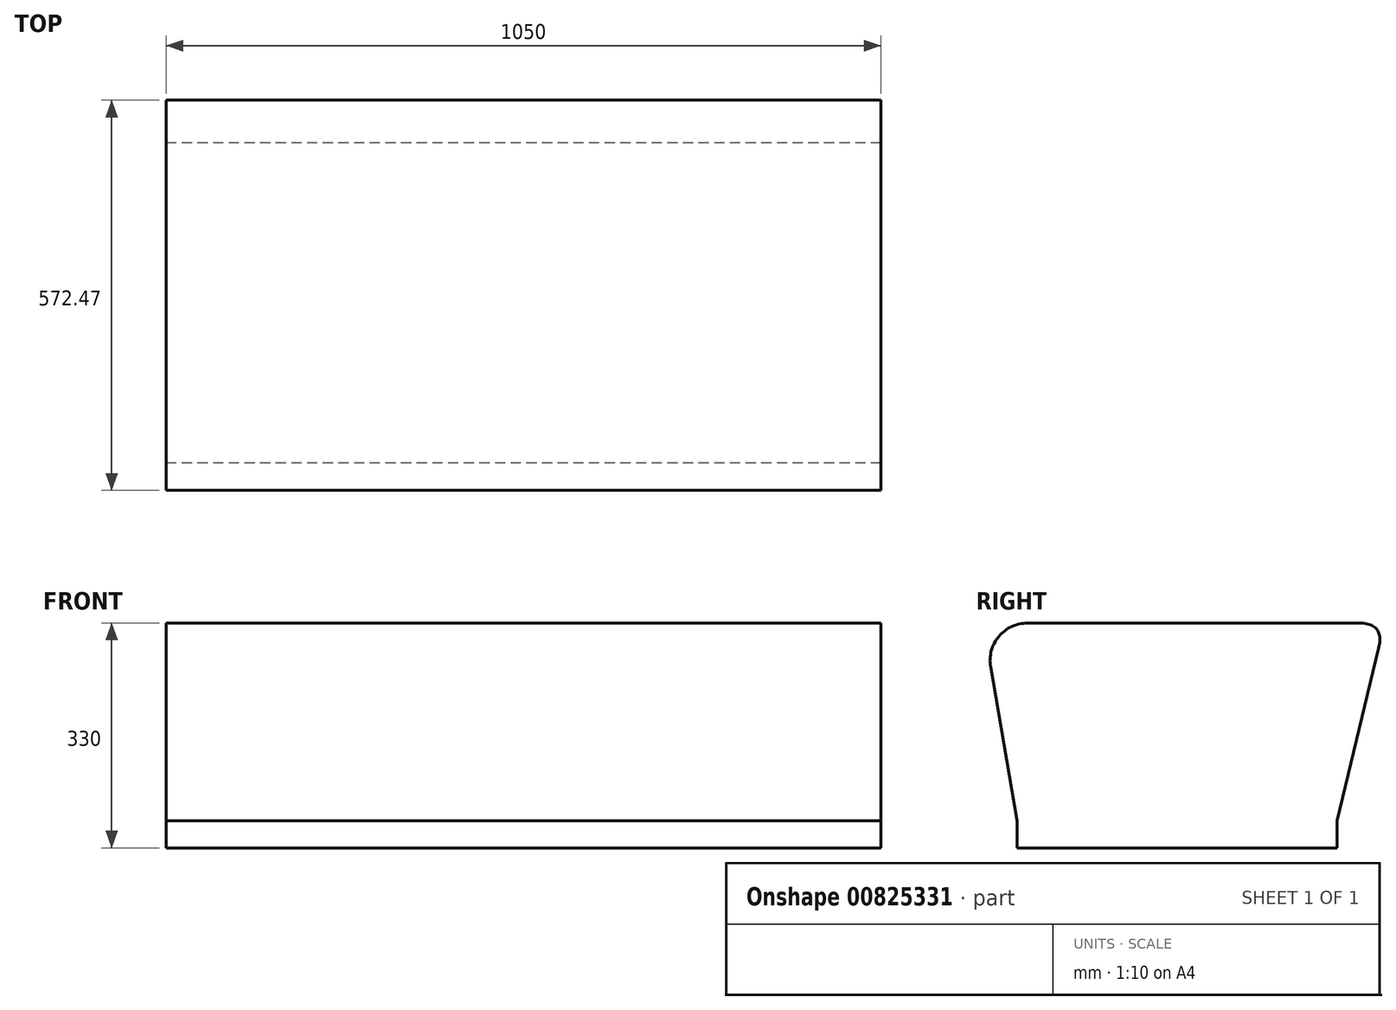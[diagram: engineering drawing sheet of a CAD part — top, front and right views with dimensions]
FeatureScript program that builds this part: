
annotation { "Feature Type Name" : "Feature", "Feature Type Description" : "" }
export const myFeature = defineFeature(function(context is Context, id is Id, definition is map)
    precondition{}
    {
        {
            var Q0;
            Q0=qCreatedBy(makeId("Right.planeOp"),FACE);
            var sketch = newSketch(context, id + "F0", { "sketchPlane" : qUnion([Q0])});
            skLineSegment(sketch, "E0", {"start": v(0, 0) * mm, "end": v(470, 0) * mm});
            skLineSegment(sketch, "E1", {"start": v(470, 0) * mm, "end": v(470, 290) * mm, "construction": true});
            skLineSegment(sketch, "E2", {"start": v(470, 290) * mm, "end": v(540, 290) * mm});
            skLineSegment(sketch, "E3", {"start": v(540, 290) * mm, "end": v(470, 290) * mm});
            skLineSegment(sketch, "E4", {"start": v(470, 290) * mm, "end": v(-50, 290) * mm});
            skLineSegment(sketch, "E5", {"start": v(-50, 290) * mm, "end": v(0, 0) * mm});
            skLineSegment(sketch, "E6", {"start": v(540, 290) * mm, "end": v(470, 0) * mm});
            skLineSegment(sketch, "E7", {"start": v(470, 0) * mm, "end": v(470, -40) * mm});
            skLineSegment(sketch, "E8", {"start": v(470, -40) * mm, "end": v(0, -40) * mm});
            skLineSegment(sketch, "E9", {"start": v(0, -40) * mm, "end": v(0, 0) * mm});
            skSolve(sketch);
        }
        {
            var Q0;
            Q0=makeQuery(id+"F0.imprint","IMPRINT",FACE,{"disambiguationData":[TD([[makeQuery(id+"F0.imprint","IMPRINT",EDGE,{"derivedFrom":sQuery(id+"F0.wireOp",EDGE,"E0")}),1.0]])]});
            var Q1;
            Q1=makeQuery(id+"F0.imprint","IMPRINT",FACE,{"disambiguationData":[TD([[makeQuery(id+"F0.imprint","IMPRINT",EDGE,{"derivedFrom":sQuery(id+"F0.wireOp",EDGE,"E0")}),-1.0]])]});
            extrude(context, id + "F1", {"entities" : qUnion([Q0, Q1]), "depth" : 1050 * mm, "offsetDistance" : 25 * mm});
        }
        {
            var Q0;
            Q0=makeQuery(id+"F1.opExtrude","SWEPT_EDGE",EDGE,{"disambiguationData":[OSD([sQuery(id+"F0.wireOp",EDGE,"E4"),sQuery(id+"F0.wireOp",EDGE,"E5")])]});
            fillet(context, id + "F2", {"entities" : qUnion([Q0]), "radius" : 55 * mm, "tangentPropagation" : true, "allowEdgeOverflow" : false});
        }
        {
            var Q0;
            Q0=makeQuery(id+"F1.opExtrude","SWEPT_EDGE",EDGE,{"disambiguationData":[OSD([sQuery(id+"F0.wireOp",EDGE,"E3"),sQuery(id+"F0.wireOp",EDGE,"E6")])]});
            fillet(context, id + "F3", {"entities" : qUnion([Q0]), "radius" : 30 * mm, "tangentPropagation" : true, "rho" : 0.5, "crossSection" : FilletCrossSection.CONIC, "allowEdgeOverflow" : false});
        }
        {
            var Q0;
            Q0=makeQuery(id+"F1.opExtrude","SWEPT_FACE",FACE,{"disambiguationData":[OSD([sQuery(id+"F0.wireOp",EDGE,"E8")])]});
            var sketch = newSketch(context, id + "F4", { "sketchPlane" : qUnion([Q0])});
            skLineSegment(sketch, "E10", {"start": v(0, -470) * mm, "end": v(525, -470) * mm, "construction": true});
            skLineSegment(sketch, "E11", {"start": v(525, -470) * mm, "end": v(525, -445) * mm, "construction": true});
            skSolve(sketch);
        }
    });
